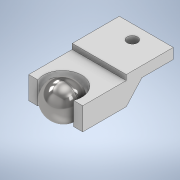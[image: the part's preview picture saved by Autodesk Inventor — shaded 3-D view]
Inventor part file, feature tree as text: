
AUTODESK INVENTOR PART (.ipt)
format: ipt  version: 2022.2 (Build 262287010, 287A)  size: 204,800 bytes
history: native  units: mm
features: sketch x4, other x3, extrude x2, hole x1
ambient origin geometry x8: Origin, YZ Plane, XZ Plane, XY Plane, X Axis, Y Axis, Z Axis, Center Point
bodies: Body1 (feature_tree), Body2 (feature_tree)
feature tree (10):
  other  "ソリッド1"
  extrude  "押し出し1"  Depth=9.0mm
  hole  "穴1"  [1 undecoded]
  extrude  "押し出し2"  Depth=3.0mm
  sketch  "スケッチ4"
  other  "フォーム1"
  sketch  "スケッチ1"
  sketch  "スケッチ2"
  sketch  "スケッチ3"
  other  "ソリッド2"
note: 1 required parameter value undecoded (feature->parameter linkage not recoverable at this tier; creation-order binding heuristic only, values carry confidence <= 0.55)
